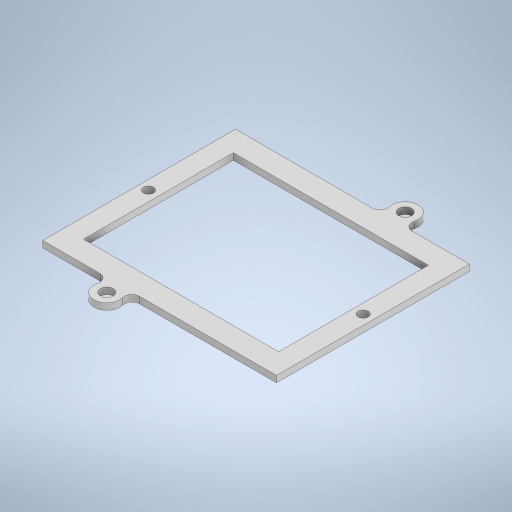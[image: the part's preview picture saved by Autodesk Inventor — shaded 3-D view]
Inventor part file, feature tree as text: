
AUTODESK INVENTOR PART (.ipt)
format: ipt  version: 2024 (Build 280153000, 153)  size: 331,264 bytes
history: native  units: in
note: dims shown in document units (in); Inventor stores cm internally (conversion verified against a paired STEP export)
features: extrude x3, plane x1, sketch x1
ambient origin geometry x8: Origin, YZ Plane, XZ Plane, XY Plane, X Axis, Y Axis, Z Axis, Center Point
bodies: Solid1 (feature_tree)
feature tree (5):
  plane  "Work Plane4"
  extrude  "Extrusion3"  Depth=0.1181in
  extrude  "Extrusion5"  Depth=0.1181in
  extrude  "Extrusion10"  Depth=0.1181in
  sketch  "Sketch9"  dims[d0=3.2874in d1=0.1181in d2=0.1181in d4=0.1969in d5=0.1969in d6=0.4724in d7=0.4724in d8=2.6575in d9=1.3287in d10=1.6437in d22=0.1181in d23=0.0in d24=0.3543in d27=0.185in d33=0.1181in d34=0.0in d43=3.9252in d44=0.1772in d87=0.0662in d90=1.2598in d92=0.3937in d94=2.7362in d96=3.563in d97=0.3543in d98=0.3543in d99=0.3937in d100=0.3937in d101=0.2362in d102=0.4724in d103=1.4567in d104=0.2756in d105=4.2717in d106=1.4075in d107=0.1181in d108=0.0in d31=0.0197in d32=0.0344in d91=0.0344in d93=0.0344in]
